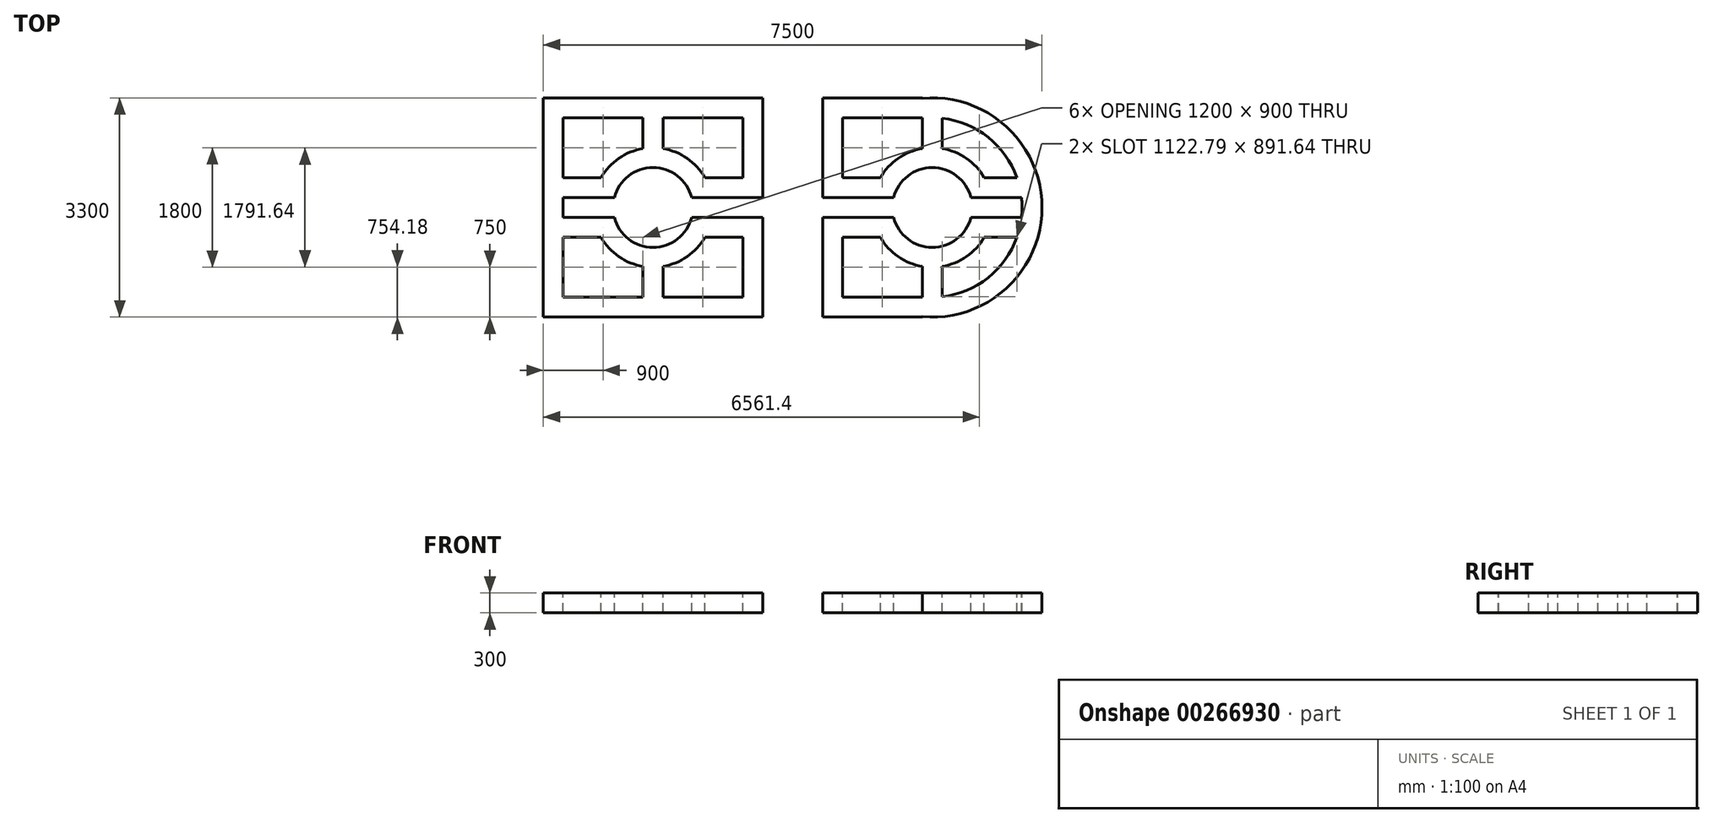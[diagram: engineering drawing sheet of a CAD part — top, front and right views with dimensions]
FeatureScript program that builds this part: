
annotation { "Feature Type Name" : "Feature", "Feature Type Description" : "" }
export const myFeature = defineFeature(function(context is Context, id is Id, definition is map)
    precondition{}
    {
        {
            var Q0;
            Q0=qCreatedBy(makeId("Top.planeOp"),FACE);
            var sketch = newSketch(context, id + "F0", { "sketchPlane" : qUnion([Q0])});
            skLineSegment(sketch, "E0.bottom", {"start": v(-1650, 1650) * mm, "end": v(1650, 1650) * mm});
            skLineSegment(sketch, "E0.top", {"start": v(-1650, -1650) * mm, "end": v(1650, -1650) * mm});
            skLineSegment(sketch, "E0.left", {"start": v(-1650, 1650) * mm, "end": v(-1650, -1650) * mm});
            skLineSegment(sketch, "E0.right", {"start": v(1650, 1650) * mm, "end": v(1650, 150) * mm});
            skPoint(sketch, "E0.middle", {"position": v(0, 0) * mm});
            skLineSegment(sketch, "E1.bottom", {"start": v(-1350, 1350) * mm, "end": v(-150, 1350) * mm});
            skLineSegment(sketch, "E1.top", {"start": v(-1350, -1350) * mm, "end": v(-150, -1350) * mm});
            skLineSegment(sketch, "E1.left", {"start": v(-1350, 1350) * mm, "end": v(-1350, 450) * mm});
            skLineSegment(sketch, "E1.right", {"start": v(1350, 1350) * mm, "end": v(1350, 450) * mm});
            skLineSegment(sketch, "E2.bottom", {"start": v(-1350, 150) * mm, "end": v(-580.95, 150) * mm});
            skLineSegment(sketch, "E2.top", {"start": v(-1350, -150) * mm, "end": v(-580.95, -150) * mm});
            skLineSegment(sketch, "E2.left", {"start": v(-1650, 150) * mm, "end": v(-1650, -191.25) * mm});
            skLineSegment(sketch, "E3.bottom", {"start": v(-1350, 450) * mm, "end": v(-779.42, 450) * mm});
            skLineSegment(sketch, "E3.top", {"start": v(-1350, -450) * mm, "end": v(-779.42, -450) * mm});
            skLineSegment(sketch, "E3.left", {"start": v(-1650, 450) * mm, "end": v(-1650, -450) * mm});
            skArc(sketch, "E4", {"start": v(580.95, 150) * mm, "mid": v(0, 600) * mm, "end": v(-580.95, 150) * mm});
            skArc(sketch, "E5", {"start": v(779.42, 450) * mm, "mid": v(513.6, 739.06) * mm, "end": v(150, 887.41) * mm});
            skLineSegment(sketch, "E6.left", {"start": v(-150, 1350) * mm, "end": v(-150, 887.41) * mm});
            skLineSegment(sketch, "E6.right", {"start": v(150, 1350) * mm, "end": v(150, 887.41) * mm});
            skLineSegment(sketch, "E7.trimOffspring", {"start": v(1350, -450) * mm, "end": v(1350, -1350) * mm});
            skArc(sketch, "E8.trimOffspring", {"start": v(-580.95, -150) * mm, "mid": v(0, -600) * mm, "end": v(580.95, -150) * mm});
            skArc(sketch, "E9.trimOffspring", {"start": v(-779.42, -450) * mm, "mid": v(-513.6, -739.06) * mm, "end": v(-150, -887.41) * mm});
            skLineSegment(sketch, "E10.trimOffspring", {"start": v(580.95, -150) * mm, "end": v(1650, -150) * mm});
            skLineSegment(sketch, "E11.trimOffspring", {"start": v(150, -887.41) * mm, "end": v(150, -1350) * mm});
            skLineSegment(sketch, "E12.trimOffspring", {"start": v(779.42, -450) * mm, "end": v(1350, -450) * mm});
            skLineSegment(sketch, "E13.trimOffspring", {"start": v(-150, -887.41) * mm, "end": v(-150, -1350) * mm});
            skArc(sketch, "E14.trimOffspring", {"start": v(150, -887.41) * mm, "mid": v(513.6, -739.06) * mm, "end": v(779.42, -450) * mm});
            skLineSegment(sketch, "E15.trimOffspring", {"start": v(150, -1350) * mm, "end": v(1650, -1350) * mm});
            skLineSegment(sketch, "E16.trimOffspring", {"start": v(779.42, 450) * mm, "end": v(1350, 450) * mm});
            skLineSegment(sketch, "E17.trimOffspring", {"start": v(580.95, 150) * mm, "end": v(1650, 150) * mm});
            skArc(sketch, "E18.trimOffspring", {"start": v(-150, 887.41) * mm, "mid": v(-513.6, 739.06) * mm, "end": v(-779.42, 450) * mm});
            skLineSegment(sketch, "E19.trimOffspring", {"start": v(-1350, 150) * mm, "end": v(-1350, -150) * mm});
            skLineSegment(sketch, "E20.trimOffspring", {"start": v(-1350, -450) * mm, "end": v(-1350, -1350) * mm});
            skLineSegment(sketch, "E21.trimOffspring", {"start": v(150, 1350) * mm, "end": v(1350, 1350) * mm});
            skPoint(sketch, "E22.trimOffspring.end.orphan", {"position": v(1650, -450) * mm});
            skPoint(sketch, "E23.orphan", {"position": v(1650, -1650) * mm});
            skPoint(sketch, "E24.orphan", {"position": v(1650, 450) * mm});
            skLineSegment(sketch, "E25.trimOffspring", {"start": v(1650, -150) * mm, "end": v(1650, -1650) * mm});
            skPoint(sketch, "E26.orphan", {"position": v(1650, 1650) * mm});
            skLineSegment(sketch, "E27", {"start": v(5850, 1484.03) * mm, "end": v(5850, -2415.26) * mm, "construction": true});
            skLineSegment(sketch, "E28", {"start": v(-1650, 0) * mm, "end": v(2550, 0) * mm, "construction": true});
            skLineSegment(sketch, "E29", {"start": v(4200, 600) * mm, "end": v(4200, -1330.54) * mm, "construction": true});
            skArc(sketch, "E30", {"start": v(3420.58, -450) * mm, "mid": v(3686.4, -739.06) * mm, "end": v(4050, -887.41) * mm});
            skArc(sketch, "E31", {"start": v(4780.95, -150) * mm, "mid": v(4200, -600) * mm, "end": v(3619.05, -150) * mm});
            skArc(sketch, "E32", {"start": v(4050, -1643.17) * mm, "mid": v(5850, 0) * mm, "end": v(4050, 1643.17) * mm});
            skPoint(sketch, "E33.orphan", {"position": v(1350, 1350) * mm});
            skArc(sketch, "E34", {"start": v(4350, -1341.64) * mm, "mid": v(5039.55, -1057.2) * mm, "end": v(5472.8, -450) * mm});
            skLineSegment(sketch, "E35", {"start": v(2550, 1650) * mm, "end": v(2550, 150) * mm});
            skLineSegment(sketch, "E36", {"start": v(2850, 1350) * mm, "end": v(2850, 450) * mm});
            skLineSegment(sketch, "E37.trimOffspring", {"start": v(2550, 1650) * mm, "end": v(4200, 1650) * mm});
            skLineSegment(sketch, "E38.trimOffspring", {"start": v(2550, -1650) * mm, "end": v(4200, -1650) * mm});
            skLineSegment(sketch, "E39.trimOffspring", {"start": v(2850, -1350) * mm, "end": v(4050, -1350) * mm});
            skLineSegment(sketch, "E40.trimOffspring", {"start": v(2850, -450) * mm, "end": v(3420.58, -450) * mm});
            skLineSegment(sketch, "E41.trimOffspring", {"start": v(2550, -150) * mm, "end": v(3619.05, -150) * mm});
            skLineSegment(sketch, "E42.trimOffspring", {"start": v(2550, 150) * mm, "end": v(3619.05, 150) * mm});
            skLineSegment(sketch, "E43.trimOffspring", {"start": v(2850, 450) * mm, "end": v(3420.58, 450) * mm});
            skLineSegment(sketch, "E44.trimOffspring", {"start": v(2850, 1350) * mm, "end": v(4050, 1350) * mm});
            skLineSegment(sketch, "E45.trimOffspring", {"start": v(2550, -150) * mm, "end": v(2550, -1650) * mm});
            skLineSegment(sketch, "E46.trimOffspring", {"start": v(2850, 0) * mm, "end": v(7106.76, 0) * mm, "construction": true});
            skLineSegment(sketch, "E47", {"start": v(4050, 1650) * mm, "end": v(4050, 1643.17) * mm});
            skLineSegment(sketch, "E48", {"start": v(4350, 1341.64) * mm, "end": v(4350, 887.41) * mm});
            skLineSegment(sketch, "E49.trimOffspring", {"start": v(4050, -1643.17) * mm, "end": v(4050, -1650) * mm});
            skLineSegment(sketch, "E50.trimOffspring", {"start": v(4050, 1350) * mm, "end": v(4050, 887.41) * mm});
            skLineSegment(sketch, "E51.trimOffspring", {"start": v(2850, -450) * mm, "end": v(2850, -1350) * mm});
            skLineSegment(sketch, "E52.trimOffspring", {"start": v(4050, -887.41) * mm, "end": v(4050, -1350) * mm});
            skLineSegment(sketch, "E53.trimOffspring", {"start": v(4350, -887.41) * mm, "end": v(4350, -1341.64) * mm});
            skPoint(sketch, "E54.orphan", {"position": v(4200, 1330.54) * mm});
            skArc(sketch, "E55.trimOffspring", {"start": v(4979.42, 450) * mm, "mid": v(4713.6, 739.06) * mm, "end": v(4350, 887.41) * mm});
            skArc(sketch, "E56.trimOffspring", {"start": v(4350, -887.41) * mm, "mid": v(4713.6, -739.06) * mm, "end": v(4979.42, -450) * mm});
            skArc(sketch, "E57.trimOffspring", {"start": v(4050, 887.41) * mm, "mid": v(3686.4, 739.06) * mm, "end": v(3420.58, 450) * mm});
            skLineSegment(sketch, "E58.trimOffspring", {"start": v(4979.42, 450) * mm, "end": v(5472.8, 450) * mm});
            skLineSegment(sketch, "E59.trimOffspring", {"start": v(4979.42, -450) * mm, "end": v(5472.8, -450) * mm});
            skArc(sketch, "E60.trimOffspring", {"start": v(3619.05, 150) * mm, "mid": v(4200, 600) * mm, "end": v(4780.95, 150) * mm});
            skLineSegment(sketch, "E61.trimOffspring", {"start": v(4780.95, 150) * mm, "end": v(5541.64, 150) * mm});
            skLineSegment(sketch, "E62.trimOffspring", {"start": v(4780.95, -150) * mm, "end": v(5541.64, -150) * mm});
            skArc(sketch, "E63.trimOffspring", {"start": v(5541.64, -150) * mm, "mid": v(5550, 0) * mm, "end": v(5541.64, 150) * mm});
            skArc(sketch, "E64.trimOffspring", {"start": v(5472.8, 450) * mm, "mid": v(5039.55, 1057.2) * mm, "end": v(4350, 1341.64) * mm});
            skLineSegment(sketch, "E65", {"start": v(0, 0) * mm, "end": v(0, -2247.96) * mm, "construction": true});
            skPoint(sketch, "E65.endSnap0", {"position": v(0, -600) * mm});
            skSolve(sketch);
        }
        {
            var Q0;
            {var subQ8=sQuery(id+"F0.wireOp",EDGE,"E0.bottom");Q0=makeQuery(id+"F0.imprint","IMPRINT",FACE,{"disambiguationData":[TD([[makeQuery(id+"F0.imprint","IMPRINT",EDGE,{"derivedFrom":subQ8}),-1.0]])]});}
            var Q1;
            Q1=makeQuery(id+"F0.imprint","IMPRINT",FACE,{"disambiguationData":[TD([[makeQuery(id+"F0.imprint","IMPRINT",EDGE,{"derivedFrom":sQuery(id+"F0.wireOp",EDGE,"E30")}),1.0]])]});
            extrude(context, id + "F1", {"entities" : qUnion([Q0, Q1]), "oppositeDirection" : true, "depth" : 300 * mm});
        }
    });
